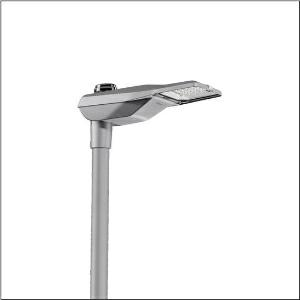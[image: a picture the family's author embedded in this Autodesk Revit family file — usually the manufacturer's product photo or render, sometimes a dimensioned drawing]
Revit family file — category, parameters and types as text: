
# Revit family: streetlight_sl_21_micro___pl52_5xe5h47n08cb_b1c0
name_source: partatom
category: Lighting Fixtures
units: mm (PartAtom-declared; Revit-internal decimal feet)

## family parameters
Cut with Voids When Loaded = No
Host = Face
Light Source = No
Part Type = Normal
Room Calculation Point = No
Round Connector Dimension = Use Diameter
Shared = No

## types (1)
- --- (1 x LED, 2340 lm, 15.8 W, 4000K)
    Apparent Load = 16 VA
    CIE Flux Codes = 27 59 98 100 100
    Color Rendering = 70
    Color Temperature = 4000K
    Default Elevation = 1800 mm
    Description = Streetlight SL 21 micro, mast luminaire, primary light control with lens, of PMMA, primary optical cover: cover, of toughened safety glass, transparent, light distribution: PL52, light emission: direct distribution, primary light characteristic: asymmetric, installation type: post-top, LED, 3G 1.5mm², High Power LED, rated luminous flux: 2.340lm, luminous efficacy: 148lm/W, light colour: 740, colour temperature: 4000K, control: overheat protection, presetting dimming linear, constant luminous flux control, time-dependent luminous flux control, flexible luminous flux parameterisation, mains connection: 230..240V, AC, 50/60Hz, connection cable pre-assembled, cable length: 6,5m, wiring characteristics: H07RN-F, start of lifetime: 16W, end of service life: 16W, reduction: 8W, luminaire housing, of diecast aluminium (EN AC-44300), powder-coated, Siteco® metallic grey (DB 702S), corrosivity category C5 mid according to DIN EN ISO 12944, multi-level sealing system, sealing non-destructively replaceable, inclination adjustable: 0°, 5°, 10°, 15°, length: 528mm, width: 235mm, height: 110mm, spigot size: 76/60mm (post-top), protection rating (complete): IP66, insulation class (complete): insulation class I (protective earthing), certification: CE, ENEC, ENEC+, VDE, impact resistance: IK09, permissible operating ambient temperature for outdoor applications: -40..+50°C, standard-compliant lighting for roads and squares, packaging unit: 1 piece

Light Distribution: PL52
    Height = 110 mm
    Lamp = 1 x LED
    Lamp Light Flux = 2340 lm
    Lamp Power = 15.8 W
    Lamp count = 1
    Length = 528 mm
    Luminous efficacy = 148 lm/W
    Manufacturer = Siteco
    ModVariant = No
    Model = 5XE5H47N08CB
    Number of Poles = 1
    OnlyDefault = Yes
    Power Factor = 1
    Product Name = Streetlight SL 21 micro | PL52
    Product group = mast luminaire | pylon top
    ProductGroupID = 6100
    Protection Class = Protection class I
    Protection Degree = IP 66
    RLX_Detail_Level = 1
    RLX_Emergency_Light_Flux = 0 lm
    RLX_Emergency_Type = 0
    RLX_Emergency_Type_DB = No
    RlxData = <blob elided: 108197 chars, md5=2c31bac7>
    Socket = socket
    Standby Power = 0 W
    System Light Flux = 2340 lm
    System Power = 16 W
    Type Comments = factory setting: luminous flux: 100 % | dim-lin: 254 | 300 mA
    Type Image = l_1294375.jpg
    URL = http://relux.com
    VarID = @adj_086537
    Voltage = 0 V
    Weight = 0.00 kg
    Width = 235 mm

## geometry (parser evidence)
native form markers: Blend x4, Sweep x10
no freeform markers — native parametric forms only
